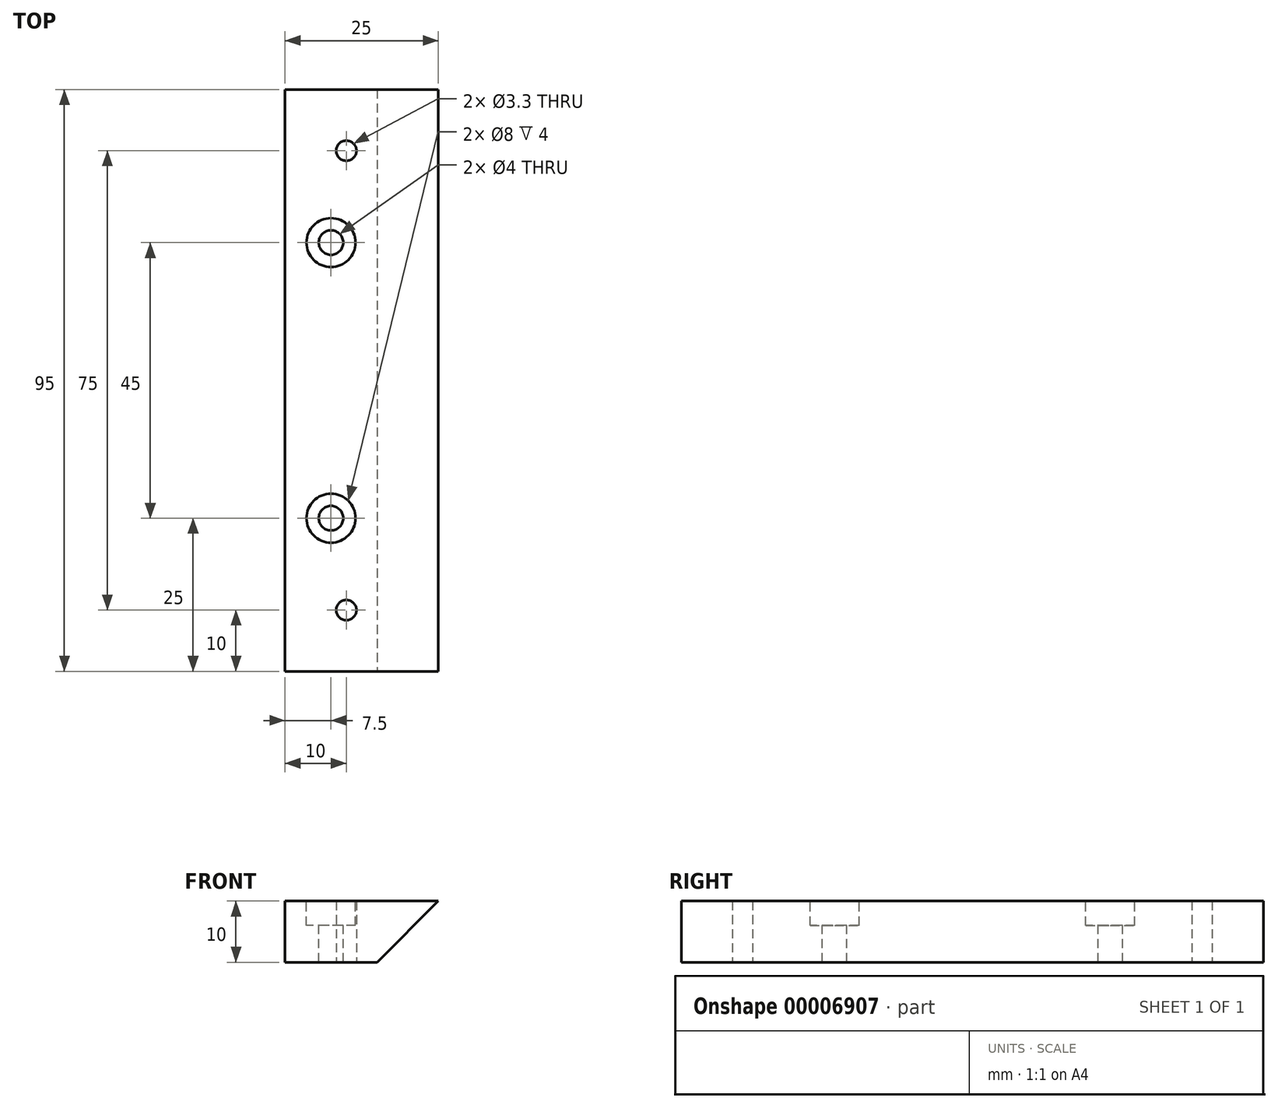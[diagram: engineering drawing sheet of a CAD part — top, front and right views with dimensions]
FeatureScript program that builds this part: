
annotation { "Feature Type Name" : "Feature", "Feature Type Description" : "" }
export const myFeature = defineFeature(function(context is Context, id is Id, definition is map)
    precondition{}
    {
        {
            var Q0;
            Q0=qCreatedBy(makeId("Top.planeOp"),FACE);
            var sketch = newSketch(context, id + "F0", { "sketchPlane" : qUnion([Q0])});
            skLineSegment(sketch, "E0.rect.bottom", {"start": v(12.5, -47.5) * mm, "end": v(-12.5, -47.5) * mm});
            skLineSegment(sketch, "E0.rect.top", {"start": v(12.5, 47.5) * mm, "end": v(-12.5, 47.5) * mm});
            skLineSegment(sketch, "E0.rect.left", {"start": v(12.5, -47.5) * mm, "end": v(12.5, 47.5) * mm});
            skLineSegment(sketch, "E0.rect.right", {"start": v(-12.5, -47.5) * mm, "end": v(-12.5, 47.5) * mm});
            skPoint(sketch, "E0.rect.middle", {"position": v(0, 0) * mm});
            skLineSegment(sketch, "E1", {"start": v(-12.5, 0) * mm, "end": v(12.5, 0) * mm, "construction": true});
            skCircle(sketch, "E2", {"center": v(-2.5, 37.5) * mm, "radius": 1.65 * mm});
            skCircle(sketch, "E3", {"center": v(-2.5, -37.5) * mm, "radius": 1.65 * mm});
            skSolve(sketch);
        }
        {
            var Q0;
            Q0=qSketchRegion(id+"F0",true);
            var Q1;
            Q1=makeQuery(id+"F0.imprint","IMPRINT",FACE,{"disambiguationData":[TD([[makeQuery(id+"F0.imprint","IMPRINT",EDGE,{"derivedFrom":sQuery(id+"F0.wireOp",EDGE,"E0.rect.bottom")}),-1.0]])]});
            extrude(context, id + "F1", {"entities" : qUnion([Q0, Q1]), "depth" : (10) * mm});
        }
        {
            var Q0;
            Q0=makeQuery(id+"F1.opExtrude","SWEPT_FACE",FACE,{"disambiguationData":[OSD([sQuery(id+"F0.wireOp",EDGE,"E0.rect.bottom")])]});
            var sketch = newSketch(context, id + "F2", { "sketchPlane" : qUnion([Q0])});
            skLineSegment(sketch, "E4", {"start": v(2.5, 0) * mm, "end": v(12.5, 10) * mm});
            skSolve(sketch);
        }
        {
            var Q0;
            Q0 = qSketchRegion(id + "F2", true);
            var Q1;
            {var subQ2=sQuery(id+"F2.wireOp",EDGE,"E4");Q1=makeQuery(id+"F2.imprint","IMPRINT",FACE,{"disambiguationData":[TD([[makeQuery(id+"F2.imprint","IMPRINT",EDGE,{"derivedFrom":subQ2}),-1.0]])]});}
            extrude(context, id + "F3", {"entities" : qUnion([Q0, Q1]), "operationType" : NewBodyOperationType.REMOVE, "endBound" : BoundingType.THROUGH_ALL, "oppositeDirection" : true, "depth" : 25 * mm});
        }
        {
            var Q0;
            Q0=makeQuery(id+"F1.opExtrude","CAP_FACE",FACE,{"disambiguationData":[OSD([sQuery(id+"F0.wireOp",EDGE,"E0.rect.bottom"),sQuery(id+"F0.wireOp",EDGE,"E0.rect.top"),sQuery(id+"F0.wireOp",EDGE,"E0.rect.left"),sQuery(id+"F0.wireOp",EDGE,"E0.rect.right"),sQuery(id+"F0.wireOp",EDGE,"E2"),sQuery(id+"F0.wireOp",EDGE,"E3")])],"isStart":false});
            var sketch = newSketch(context, id + "F4", { "sketchPlane" : qUnion([Q0])});
            skCircle(sketch, "E5", {"center": v(-5, 22.5) * mm, "radius": 4 * mm});
            skCircle(sketch, "E6", {"center": v(-5, -22.5) * mm, "radius": 4 * mm});
            skSolve(sketch);
        }
        {
            var Q0;
            Q0=makeQuery(id+"F4.imprint","IMPRINT",FACE,{"disambiguationData":[TD([[makeQuery(id+"F4.imprint","IMPRINT",EDGE,{"derivedFrom":sQuery(id+"F4.wireOp",EDGE,"E6")}),1.0]])]});
            var Q1;
            Q1=makeQuery(id+"F4.imprint","IMPRINT",FACE,{"disambiguationData":[TD([[makeQuery(id+"F4.imprint","IMPRINT",EDGE,{"derivedFrom":sQuery(id+"F4.wireOp",EDGE,"E5")}),1.0]])]});
            extrude(context, id + "F5", {"entities" : qUnion([Q0, Q1]), "operationType" : NewBodyOperationType.REMOVE, "oppositeDirection" : true, "depth" : (4) * mm});
        }
        {
            var Q0;
            Q0=makeQuery(id+"F5.boolean.opBoolean","COPY",FACE,{"derivedFrom":makeQuery(id+"F5.opExtrude","CAP_FACE",FACE,{"disambiguationData":[OSD([sQuery(id+"F4.wireOp",EDGE,"E6")])],"isStart":false})});
            var sketch = newSketch(context, id + "F6", { "sketchPlane" : qUnion([Q0])});
            skCircle(sketch, "E7", {"center": v(-5, -22.5) * mm, "radius": 2 * mm});
            skSolve(sketch);
        }
        {
            var Q0;
            Q0 = qSketchRegion(id + "F6", true);
            extrude(context, id + "F7", {"entities" : qUnion([Q0]), "operationType" : NewBodyOperationType.REMOVE, "oppositeDirection" : true, "depth" : 25 * mm});
        }
        {
            var Q0;
            Q0=makeQuery(id+"F5.boolean.opBoolean","COPY",FACE,{"derivedFrom":makeQuery(id+"F5.opExtrude","CAP_FACE",FACE,{"disambiguationData":[OSD([sQuery(id+"F4.wireOp",EDGE,"E5")])],"isStart":false})});
            var sketch = newSketch(context, id + "F8", { "sketchPlane" : qUnion([Q0])});
            skCircle(sketch, "E8", {"center": v(-5, 22.5) * mm, "radius": 2 * mm});
            skSolve(sketch);
        }
        {
            var Q0;
            Q0 = qSketchRegion(id + "F8", true);
            extrude(context, id + "F9", {"entities" : qUnion([Q0]), "operationType" : NewBodyOperationType.REMOVE, "oppositeDirection" : true, "depth" : 25 * mm});
        }
    });
